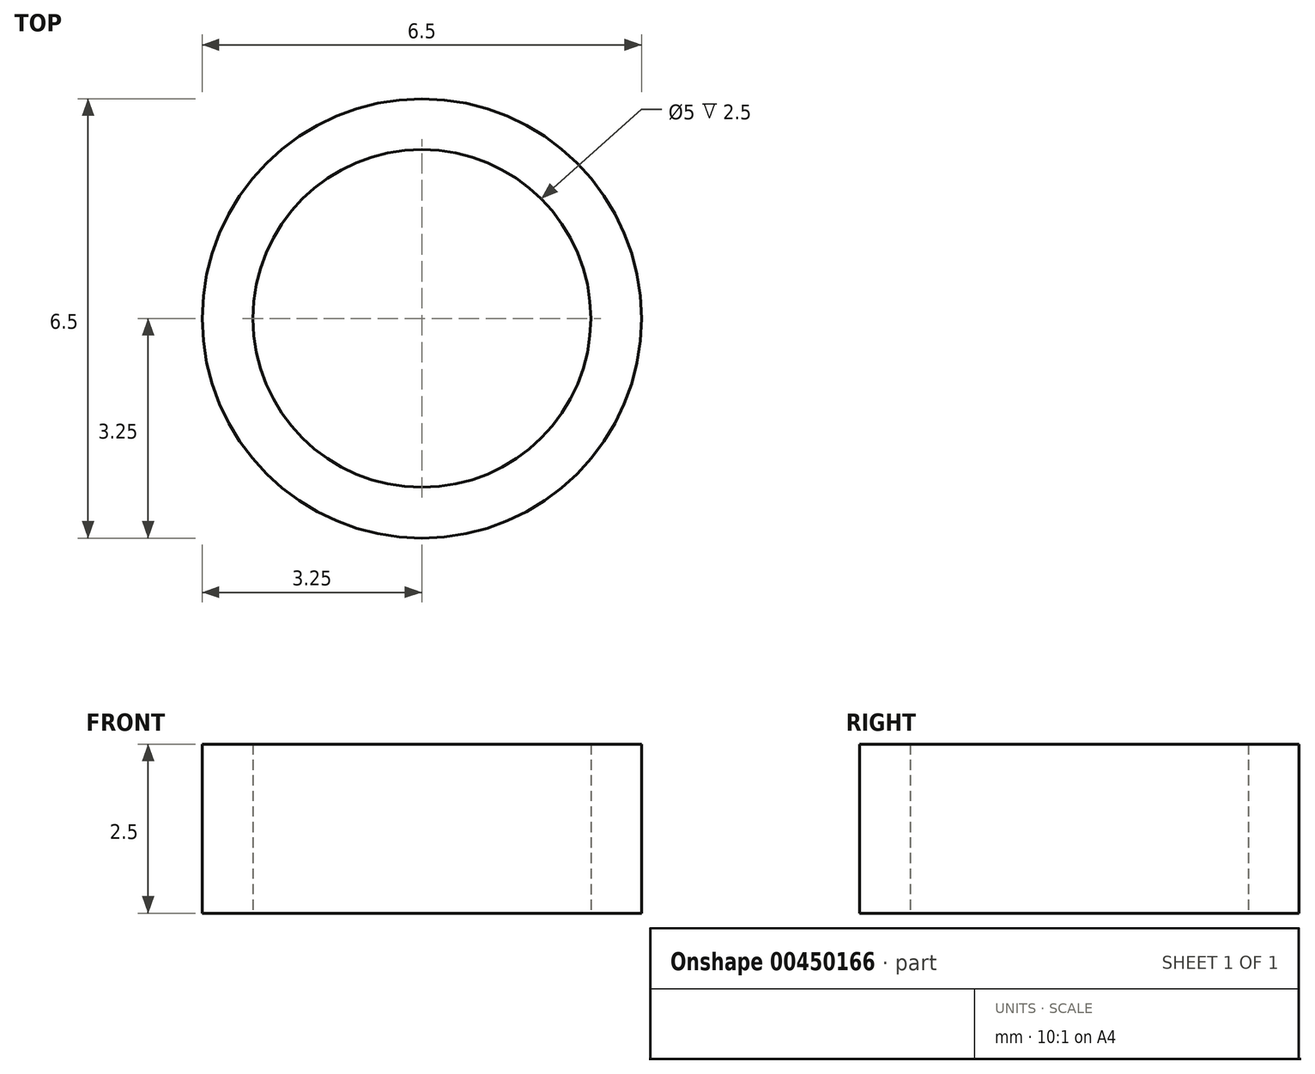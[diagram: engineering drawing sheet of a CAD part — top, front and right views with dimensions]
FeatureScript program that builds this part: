
annotation { "Feature Type Name" : "Feature", "Feature Type Description" : "" }
export const myFeature = defineFeature(function(context is Context, id is Id, definition is map)
    precondition{}
    {
        {
            var Q0;
            Q0=qCreatedBy(makeId("Top.planeOp"),FACE);
            var sketch = newSketch(context, id + "F0", { "sketchPlane" : qUnion([Q0])});
            skCircle(sketch, "E0", {"center": v(0, 0) * mm, "radius": 2.5 * mm});
            skCircle(sketch, "E1.0", {"center": v(0, 0) * mm, "radius": 3.25 * mm});
            skSolve(sketch);
        }
        {
            var Q0;
            Q0 = qSketchRegion(id + "F0", true);
            extrude(context, id + "F1", {"entities" : qUnion([Q0]), "depth" : 2.5 * mm});
        }
    });
